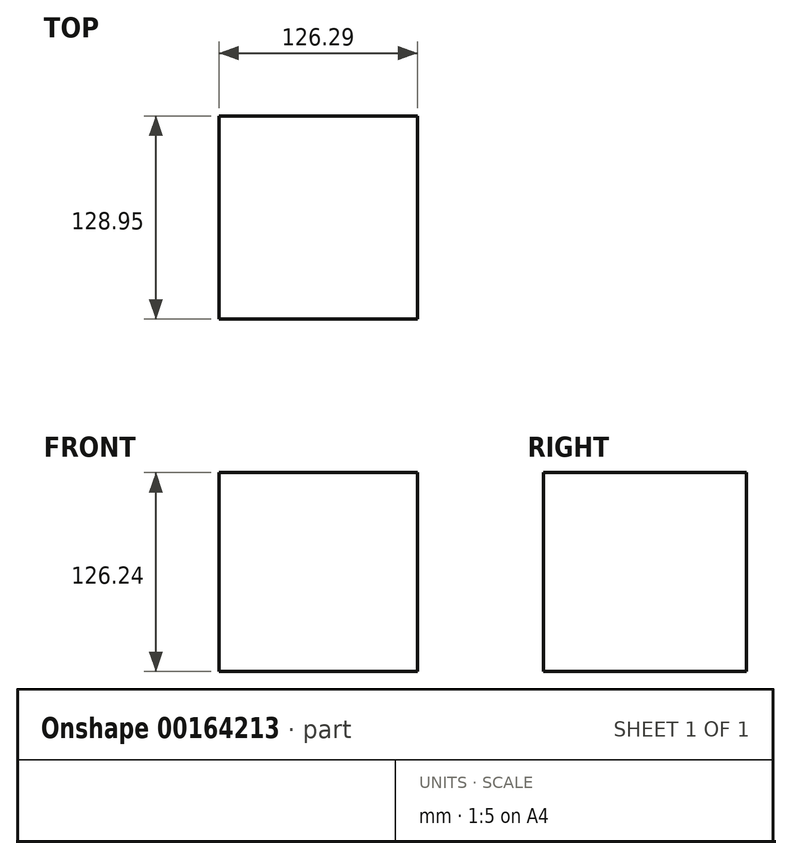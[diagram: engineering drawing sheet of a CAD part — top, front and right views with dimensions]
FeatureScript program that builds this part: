
annotation { "Feature Type Name" : "Feature", "Feature Type Description" : "" }
export const myFeature = defineFeature(function(context is Context, id is Id, definition is map)
    precondition{}
    {
        {
            var Q0;
            Q0=qCreatedBy(makeId("Top.planeOp"),FACE);
            var sketch = newSketch(context, id + "F0", { "sketchPlane" : qUnion([Q0])});
            skLineSegment(sketch, "E0", {"start": v(0, 0) * mm, "end": v(0, 128.95) * mm});
            skLineSegment(sketch, "E1", {"start": v(0, 128.95) * mm, "end": v(126.3, 128.95) * mm});
            skLineSegment(sketch, "E2", {"start": v(126.3, 128.95) * mm, "end": v(126.3, 0) * mm});
            skLineSegment(sketch, "E3", {"start": v(126.3, 0) * mm, "end": v(0, 0) * mm});
            skSolve(sketch);
        }
        {
            var Q0;
            Q0=makeQuery(id+"F0.imprint","IMPRINT",FACE,{"disambiguationData":[TD([[makeQuery(id+"F0.imprint","IMPRINT",EDGE,{"derivedFrom":sQuery(id+"F0.wireOp",EDGE,"E0")}),-1.0]])]});
            extrude(context, id + "F1", {"entities" : qUnion([Q0]), "depth" : 126.24 * mm});
        }
    });
